# Revit family: BC_Hitachi_RPC-FSR-1.5-6.0_LOD200
name_source: partatom
category: Mechanical Equipment
revit_build: Autodesk Revit 2018 (Build: 20170223_1515(x64)
units: mm (PartAtom-declared; Revit-internal decimal feet)

## family parameters
Cut with Voids When Loaded = No
Host = Face
OmniClass Number = 23.75.70.00
OmniClass Title = HVAC Distribution Devices
Part Type = Normal
Room Calculation Point = No
Round Connector Dimension = Use Diameter
Shared = No

## types (1)
- BC_Hitachi_RPC-FSR-1.5-6.0_LOD200
    Acoustic Pressure Level Maxi = 37
    Acoustic Pressure Level Mini = 28
    Air Flow(HiH/Hi/Me/low) m3/min = 15/13/11/9
    BC_OBJECT_ID = 209120
    BC_OBJECT_VERSION = #8
    BC_VARIANT_ID = 508776
    Color = Spring white (4.1Y8.5/0.7)
    Cooling Capacity = 0 kW
    Default Elevation = 1219.20 mm
    Description = RPC-FSR - Ceiling type
    Drain distance = 222.00 mm
    Drain pipe Height = 40.00 mm
    Fan motor type (output) = 50 W
    Frequency = 50 Hz
    Gas Diameter = 12.70 mm
    Gas distance = 94.00 mm
    Gas pipe Height = 107.00 mm
    Heating Capacity = 0 kW
    Liquid Diameter = 6.35 mm
    Liquid distance = 146.00 mm
    Liquid pipe Height = 117.00 mm
    Manufacturer = Hitachi Air Conditioning Europe SAS
    Mass = 26.00 kg
    MasterFormat = Indoor Central-Station Air-Handling Units
    Masterformat Code = 23 73 00
    Maximum AC Voltage = 253 V
    Maximum Air Flow = 15000.0 L/min
    Minimum AC Voltage = 207 V
    Minimum Air Flow = 9000.0 L/min
    Model = RPC-FSR - Ceiling type
    Name BIM&CO = Indoor Unit
    Nominal Voltage = 230 V
    Number of Poles = 1
    OmniClass code = 23-33 25 00
    OmniClass description = Air Handling Units
    Outlet Diameter = 25.00 mm
    Overall depth = 690.00 mm
    Overall height = 235.00 mm
    Overall width = 960.00 mm
    Product Code = 60279267
    Reference = RPC-1.5FSR
    Refrigerant Type = R410A / R32
    Sound power max = 53
    Type Comments = RPC-1.5FSR
    Uniformat = Distribution Systems
    Uniformat code = D3040
    Usage Current = 5 A
